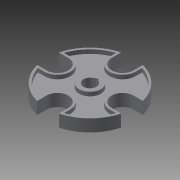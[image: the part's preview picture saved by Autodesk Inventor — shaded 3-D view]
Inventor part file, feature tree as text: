
AUTODESK INVENTOR PART (.ipt)
format: ipt  version: 2015 (Build 190159000, 159)  size: 194,560 bytes
history: native  units: mm
features: extrude x3, sketch x3, pattern_linear x1
ambient origin geometry x8: Origin, YZ Plane, XZ Plane, XY Plane, X Axis, Y Axis, Z Axis, Center Point
bodies: 实体1 (feature_tree)
feature tree (7):
  extrude  "拉伸1"  Depth=50.0mm
  extrude  "拉伸2"  Depth=9.361143mm
  pattern_linear  "矩形阵列1"  Count1=4 Spacing1=360.0deg
  extrude  "拉伸3"  Depth=28.0mm TaperAngle=0.0deg
  sketch  "草图1"  dims[d0=50.0mm d1=200.0mm]
  sketch  "草图2"  dims[d2=9.402163mm d3=9.361143mm d4=40.0mm d6=360.0deg]
  sketch  "草图3"  dims[d12=100.0mm d13=28.0mm d14=0.0mm d15=50.0mm d16=190.0mm d17=5.0mm d18=40.0mm d20=360.0deg d22=95.0mm d23=9.0mm d24=0.0mm d25=20.0mm d27=19.0mm d28=30.0mm d29=17.2mm d30=8.0mm d31=28.0mm d32=0.0mm]
